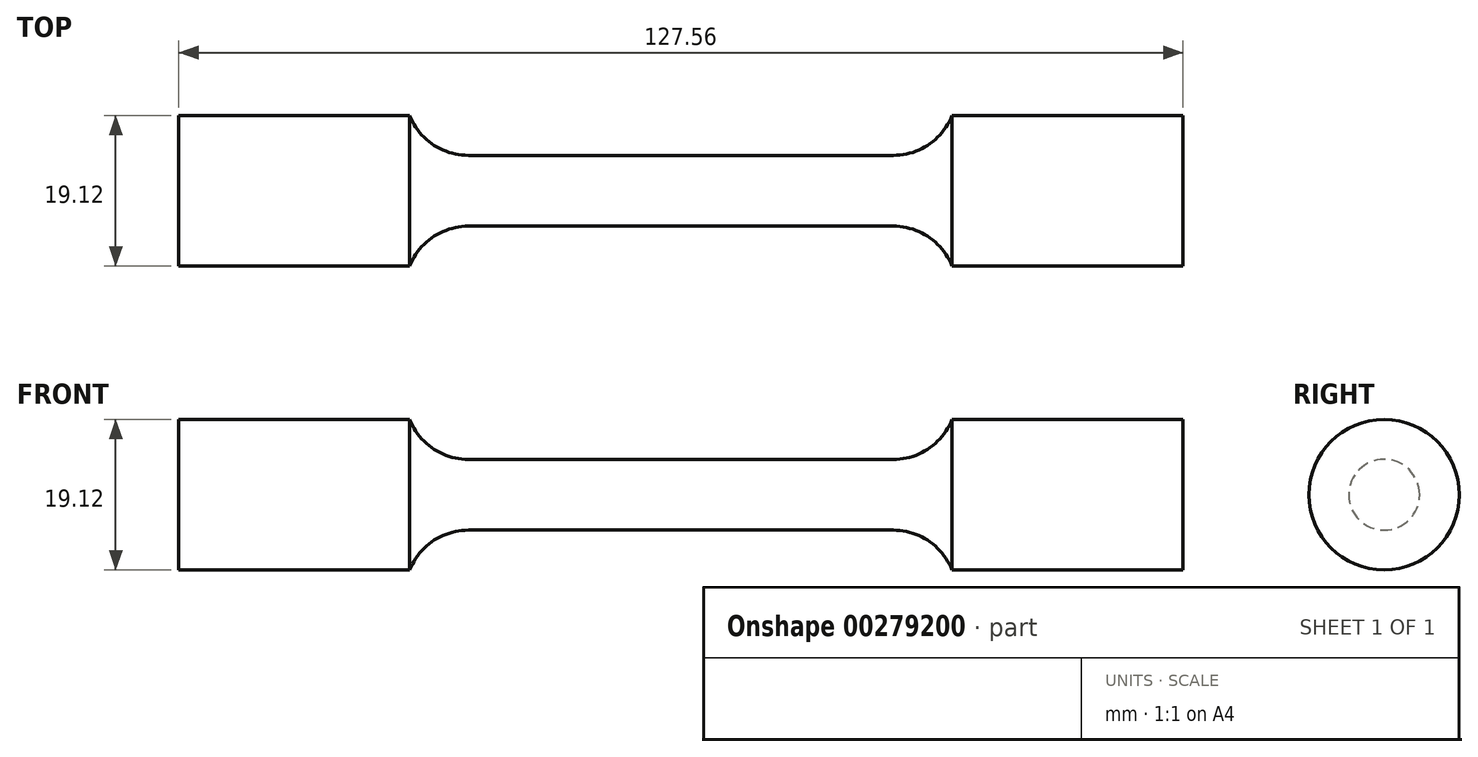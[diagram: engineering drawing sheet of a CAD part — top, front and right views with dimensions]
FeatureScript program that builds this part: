
annotation { "Feature Type Name" : "Feature", "Feature Type Description" : "" }
export const myFeature = defineFeature(function(context is Context, id is Id, definition is map)
    precondition{}
    {
        {
            var Q0;
            Q0=qCreatedBy(makeId("Front.planeOp"),FACE);
            var sketch = newSketch(context, id + "F0", { "sketchPlane" : qUnion([Q0])});
            skLineSegment(sketch, "E0", {"start": v(0, 4.5) * mm, "end": v(27, 4.5) * mm});
            skArc(sketch, "E1", {"start": v(27, 4.5) * mm, "mid": v(31.5, 5.88) * mm, "end": v(34.44, 9.56) * mm});
            skLineSegment(sketch, "E2", {"start": v(34.44, 9.56) * mm, "end": v(63.78, 9.56) * mm});
            skLineSegment(sketch, "E3", {"start": v(63.78, 0) * mm, "end": v(63.78, 9.56) * mm});
            skLineSegment(sketch, "E4.MirrorCS", {"start": v(0, 4.5) * mm, "end": v(-27, 4.5) * mm});
            skLineSegment(sketch, "E5.MirrorCS", {"start": v(-63.78, 0) * mm, "end": v(-63.78, 9.56) * mm});
            skLineSegment(sketch, "E6.MirrorCS", {"start": v(-34.44, 9.56) * mm, "end": v(-63.78, 9.56) * mm});
            skArc(sketch, "E7.MirrorCS", {"start": v(-27, 4.5) * mm, "mid": v(-31.5, 5.88) * mm, "end": v(-34.44, 9.56) * mm});
            skLineSegment(sketch, "E8", {"start": v(-63.78, 0) * mm, "end": v(63.78, 0) * mm});
            skSolve(sketch);
        }
        {
            var Q0;
            Q0=makeQuery(id+"F0.imprint","IMPRINT",FACE,{"disambiguationData":[TD([[makeQuery(id+"F0.imprint","IMPRINT",EDGE,{"derivedFrom":sQuery(id+"F0.wireOp",EDGE,"E0")}),-1.0]])]});
            var Q1;
            Q1=sQuery(id+"F0.wireOp",EDGE,"E8");
            revolve(context, id + "F1", {"entities" : qUnion([Q0]), "axis" : qUnion([Q1]), "revolveType" : RevolveType.FULL});
        }
    });
